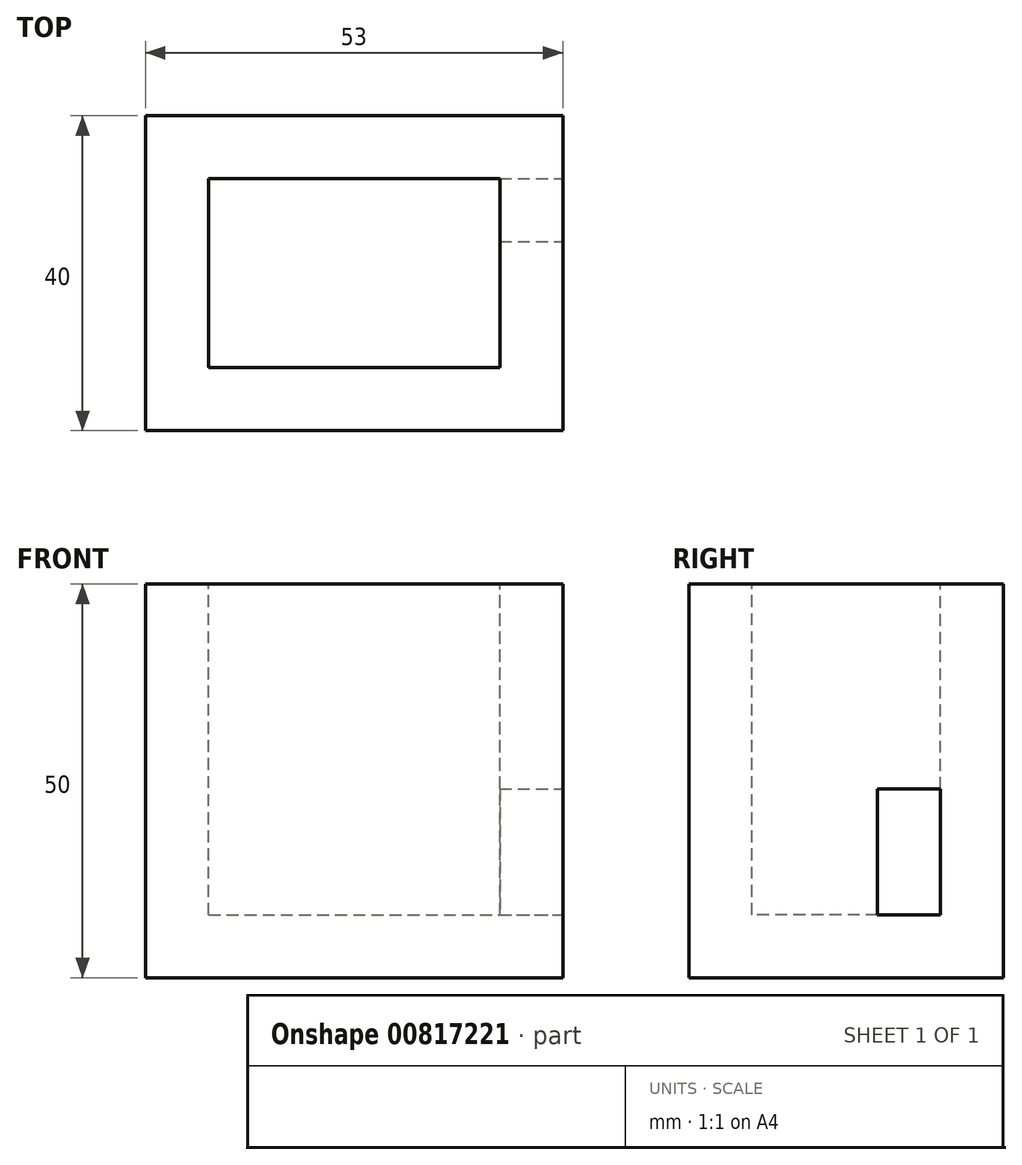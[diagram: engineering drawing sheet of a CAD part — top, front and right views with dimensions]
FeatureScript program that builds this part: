
annotation { "Feature Type Name" : "Feature", "Feature Type Description" : "" }
export const myFeature = defineFeature(function(context is Context, id is Id, definition is map)
    precondition{}
    {
        {
            var Q0;
            Q0=qCreatedBy(makeId("Top.planeOp"),FACE);
            var sketch = newSketch(context, id + "F0", { "sketchPlane" : qUnion([Q0])});
            skLineSegment(sketch, "E0.bottom", {"start": v(0, 0) * mm, "end": v(53, 0) * mm});
            skLineSegment(sketch, "E0.top", {"start": v(0, 40) * mm, "end": v(53, 40) * mm});
            skLineSegment(sketch, "E0.left", {"start": v(0, 0) * mm, "end": v(0, 40) * mm});
            skLineSegment(sketch, "E0.right", {"start": v(53, 0) * mm, "end": v(53, 40) * mm});
            skSolve(sketch);
        }
        {
            var Q0;
            Q0 = qSketchRegion(id + "F0", true);
            extrude(context, id + "F1", {"entities" : qUnion([Q0]), "depth" : 50 * mm, "offsetDistance" : 25 * mm});
        }
        {
            var Q0;
            Q0=makeQuery(id+"F1.opExtrude","CAP_FACE",FACE,{"disambiguationData":[OSD([sQuery(id+"F0.wireOp",EDGE,"E0.bottom"),sQuery(id+"F0.wireOp",EDGE,"E0.top"),sQuery(id+"F0.wireOp",EDGE,"E0.left"),sQuery(id+"F0.wireOp",EDGE,"E0.right")])],"isStart":false});
            var sketch = newSketch(context, id + "F2", { "sketchPlane" : qUnion([Q0])});
            skLineSegment(sketch, "E1.bottom", {"start": v(8, 32) * mm, "end": v(45, 32) * mm});
            skLineSegment(sketch, "E1.top", {"start": v(8, 8) * mm, "end": v(45, 8) * mm});
            skLineSegment(sketch, "E1.left", {"start": v(8, 32) * mm, "end": v(8, 8) * mm});
            skLineSegment(sketch, "E1.right", {"start": v(45, 32) * mm, "end": v(45, 8) * mm});
            skSolve(sketch);
        }
        {
            var Q0;
            Q0 = qSketchRegion(id + "F2", true);
            extrude(context, id + "F3", {"entities" : qUnion([Q0]), "operationType" : NewBodyOperationType.REMOVE, "oppositeDirection" : true, "depth" : 42 * mm, "offsetDistance" : 25 * mm});
        }
        {
            var Q0;
            Q0=makeQuery(id+"F1.opExtrude","SWEPT_FACE",FACE,{"disambiguationData":[OSD([sQuery(id+"F0.wireOp",EDGE,"E0.right")])]});
            var sketch = newSketch(context, id + "F4", { "sketchPlane" : qUnion([Q0])});
            skLineSegment(sketch, "E2.bottom", {"start": v(24, 24) * mm, "end": v(32, 24) * mm});
            skLineSegment(sketch, "E2.top", {"start": v(24, 8) * mm, "end": v(32, 8) * mm});
            skLineSegment(sketch, "E2.left", {"start": v(24, 24) * mm, "end": v(24, 8) * mm});
            skLineSegment(sketch, "E2.right", {"start": v(32, 24) * mm, "end": v(32, 8) * mm});
            skSolve(sketch);
        }
        {
            var Q0;
            Q0=makeQuery(id+"F4.imprint","IMPRINT",FACE,{"disambiguationData":[TD([[makeQuery(id+"F4.imprint","IMPRINT",EDGE,{"derivedFrom":sQuery(id+"F4.wireOp",EDGE,"E2.bottom")}),-1.0]])]});
            var Q1;
            Q1=makeQuery(id+"F3.boolean.opBoolean","COPY",FACE,{"derivedFrom":makeQuery(id+"F3.opExtrude","SWEPT_FACE",FACE,{"disambiguationData":[OSD([sQuery(id+"F2.wireOp",EDGE,"E1.right")])]})});
            extrude(context, id + "F5", {"entities" : qUnion([Q0]), "operationType" : NewBodyOperationType.REMOVE, "endBound" : BoundingType.UP_TO_SURFACE, "oppositeDirection" : true, "depth" : 25 * mm, "endBoundEntityFace" : qUnion([Q1]), "offsetDistance" : 25 * mm});
        }
    });
